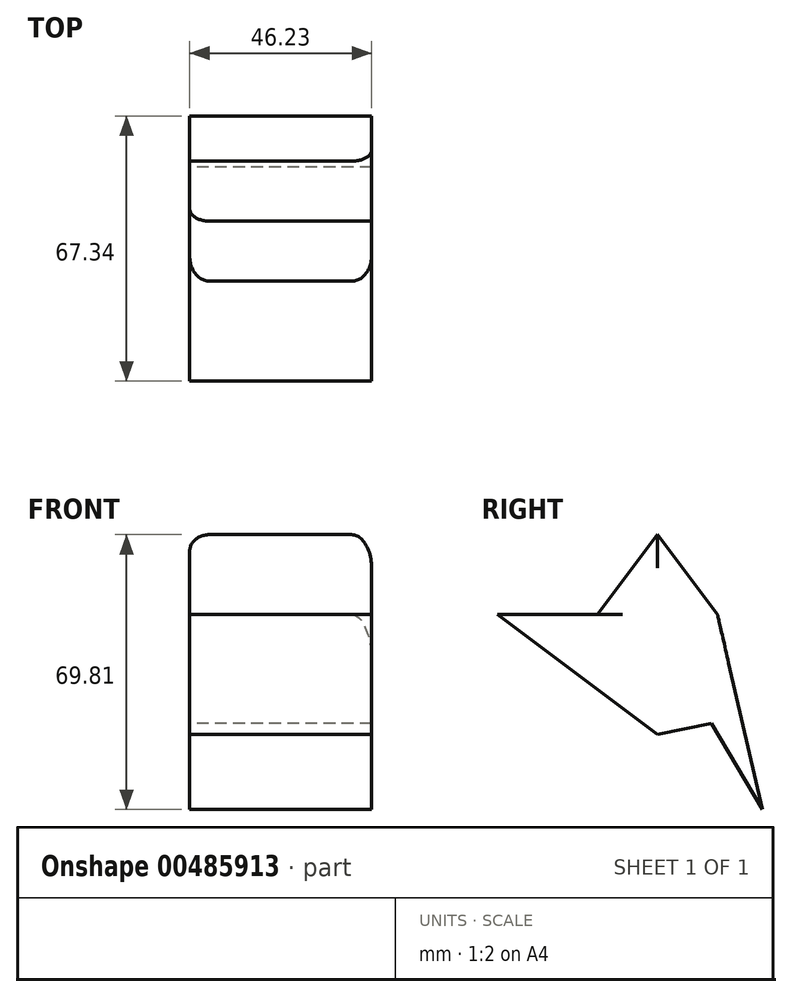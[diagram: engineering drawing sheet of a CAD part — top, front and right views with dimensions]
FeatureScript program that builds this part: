
annotation { "Feature Type Name" : "Feature", "Feature Type Description" : "" }
export const myFeature = defineFeature(function(context is Context, id is Id, definition is map)
    precondition{}
    {
        {
            var Q0;
            Q0=qCreatedBy(makeId("Right.planeOp"),FACE);
            var sketch = newSketch(context, id + "F0", { "sketchPlane" : qUnion([Q0])});
            skLineSegment(sketch, "E0", {"start": v(0, 0) * mm, "end": v(-40.64, 30.48) * mm});
            skLineSegment(sketch, "E1", {"start": v(-40.64, 30.48) * mm, "end": v(-15.24, 30.48) * mm});
            skLineSegment(sketch, "E2", {"start": v(-15.24, 30.48) * mm, "end": v(0, 50.8) * mm});
            skLineSegment(sketch, "E3", {"start": v(0, 50.8) * mm, "end": v(15.24, 30.48) * mm});
            skLineSegment(sketch, "E4", {"start": v(15.24, 30.48) * mm, "end": v(26.7, -19.01) * mm});
            skLineSegment(sketch, "E5", {"start": v(26.7, -19.01) * mm, "end": v(13.72, 2.82) * mm});
            skLineSegment(sketch, "E6", {"start": v(13.72, 2.82) * mm, "end": v(0, 0) * mm});
            skLineSegment(sketch, "E7", {"start": v(-29.93, -15.25) * mm, "end": v(-14.18, 10.64) * mm});
            skLineSegment(sketch, "E8", {"start": v(-29.93, -15.25) * mm, "end": v(2.05, 0.42) * mm, "construction": true});
            skSolve(sketch);
        }
        {
            var Q0;
            {var subQ0=sQuery(id+"F0.wireOp",EDGE,"E1");Q0=makeQuery(id+"F0.imprint","IMPRINT",FACE,{"disambiguationData":[TD([[makeQuery(id+"F0.imprint","IMPRINT",EDGE,{"derivedFrom":subQ0}),-1.0]])]});}
            extrude(context, id + "F1", {"entities" : qUnion([Q0]), "depth" : 46.23 * mm});
        }
        {
            var Q0;
            Q0=makeQuery(id+"F1.opExtrude","CAP_EDGE",EDGE,{"disambiguationData":[OSD([sQuery(id+"F0.wireOp",EDGE,"E2")])],"isStart":true});
            var Q1;
            Q1=makeQuery(id+"F1.opExtrude","CAP_EDGE",EDGE,{"disambiguationData":[OSD([sQuery(id+"F0.wireOp",EDGE,"E2")])],"isStart":false});
            var Q2;
            Q2=makeQuery(id+"F1.opExtrude","CAP_EDGE",EDGE,{"disambiguationData":[OSD([sQuery(id+"F0.wireOp",EDGE,"E3")])],"isStart":false});
            fillet(context, id + "F2", {"entities" : qUnion([Q0, Q1, Q2]), "radius" : 5.08 * mm, "tangentPropagation" : true, "allowEdgeOverflow" : false});
        }
    });
